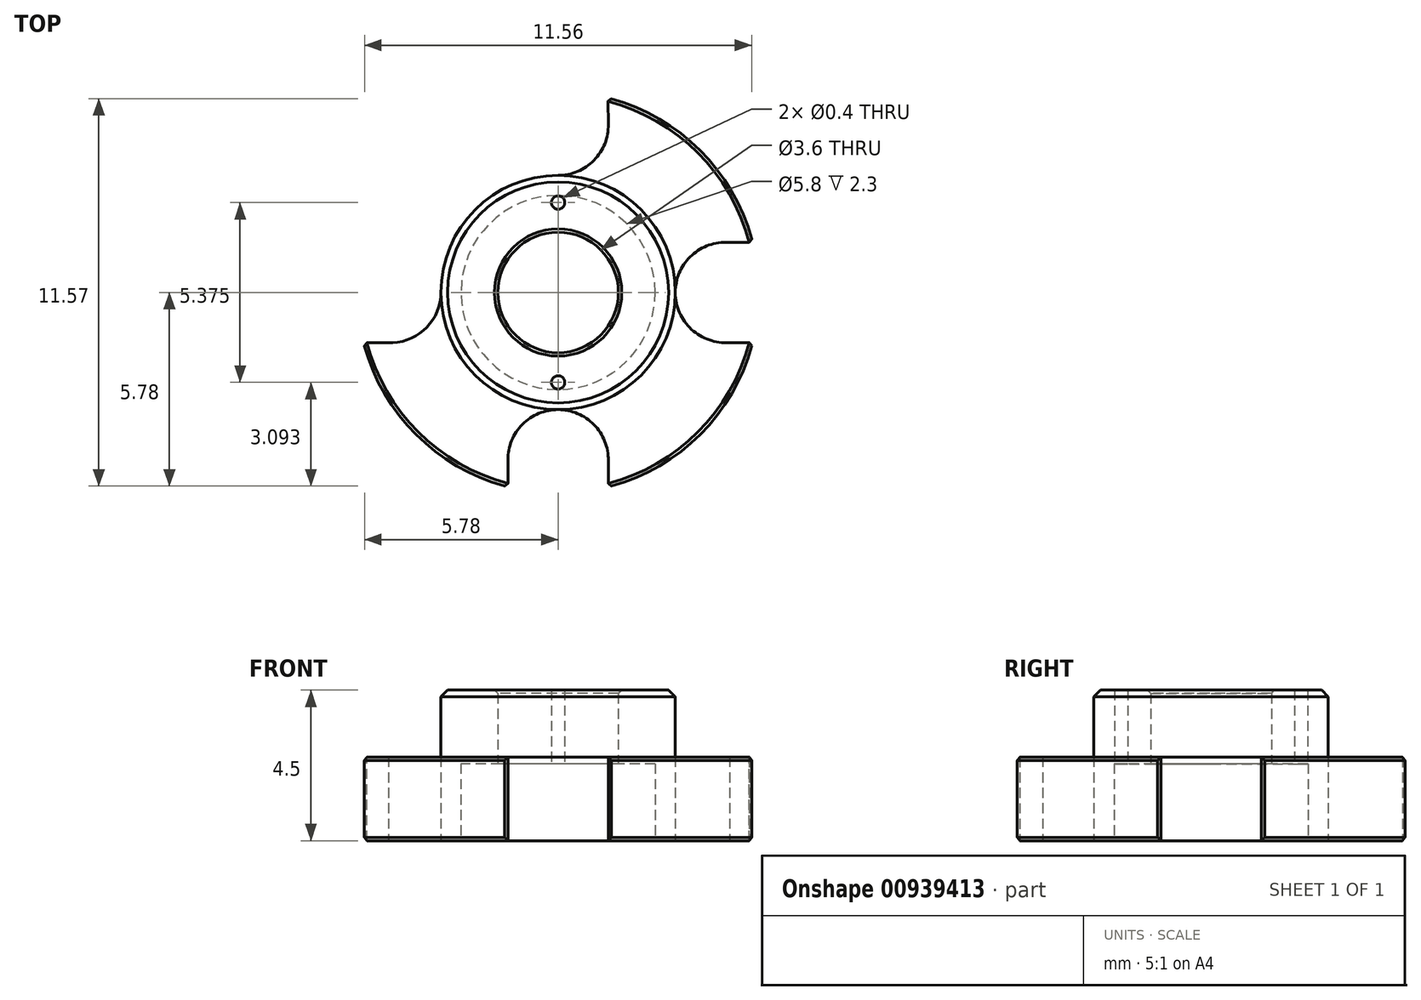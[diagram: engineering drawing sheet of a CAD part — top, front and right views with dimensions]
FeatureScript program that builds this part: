
annotation { "Feature Type Name" : "Feature", "Feature Type Description" : "" }
export const myFeature = defineFeature(function(context is Context, id is Id, definition is map)
    precondition{}
    {
        {
            var Q0;
            Q0=qCreatedBy(makeId("Top.planeOp"),FACE);
            var sketch = newSketch(context, id + "F0", { "sketchPlane" : qUnion([Q0])});
            skCircle(sketch, "E0", {"center": v(0, 0) * mm, "radius": 6 * mm});
            skCircle(sketch, "E1", {"center": v(0, 0) * mm, "radius": 3.5 * mm});
            skCircle(sketch, "E2", {"center": v(0, 0) * mm, "radius": 1.8 * mm});
            skCircle(sketch, "E3", {"center": v(0, 5) * mm, "radius": 1.5 * mm});
            skLineSegment(sketch, "E4", {"start": v(-1.5, 5.01) * mm, "end": v(-1.5, 5.8) * mm});
            skLineSegment(sketch, "E5", {"start": v(1.5, 5.03) * mm, "end": v(1.48, 5.81) * mm});
            skCircle(sketch, "E6", {"center": v(-5, 0) * mm, "radius": 1.5 * mm});
            skLineSegment(sketch, "E7", {"start": v(-4.98, 1.5) * mm, "end": v(-5.8, 1.5) * mm});
            skLineSegment(sketch, "E8", {"start": v(-4.94, -1.5) * mm, "end": v(-5.8, -1.5) * mm});
            skCircle(sketch, "E9", {"center": v(5, 0) * mm, "radius": 1.5 * mm});
            skLineSegment(sketch, "E10", {"start": v(5.01, 1.5) * mm, "end": v(5.8, 1.5) * mm});
            skLineSegment(sketch, "E11", {"start": v(5.12, -1.5) * mm, "end": v(5.81, -1.5) * mm});
            skCircle(sketch, "E12", {"center": v(0, -5) * mm, "radius": 1.5 * mm});
            skLineSegment(sketch, "E13", {"start": v(-1.5, -5) * mm, "end": v(-1.5, -5.8) * mm});
            skLineSegment(sketch, "E14", {"start": v(1.5, -5.02) * mm, "end": v(1.5, -5.8) * mm});
            skCircle(sketch, "E15", {"center": v(0, 0) * mm, "radius": 2.9 * mm});
            skCircle(sketch, "E16", {"center": v(0, 0) * mm, "radius": 2.69 * mm});
            skCircle(sketch, "E17", {"center": v(0, -2.69) * mm, "radius": 0.2 * mm});
            skCircle(sketch, "E18", {"center": v(0, 2.69) * mm, "radius": 0.2 * mm});
            skSolve(sketch);
        }
        {
            var Q0;
            Q0=makeQuery(id+"F0.imprint","IMPRINT",FACE,{"disambiguationData":[TD([[makeQuery(id+"F0.imprint","IMPRINT",EDGE,{"derivedFrom":sQuery(id+"F0.wireOp",EDGE,"E15")}),-1.0]])]});
            var Q1;
            Q1=makeQuery(id+"F0.imprint","IMPRINT",FACE,{"disambiguationData":[TD([[makeQuery(id+"F0.imprint","IMPRINT",EDGE,{"derivedFrom":sQuery(id+"F0.wireOp",EDGE,"E2")}),-1.0]])]});
            var Q2;
            Q2=makeQuery(id+"F0.imprint","IMPRINT",FACE,{"disambiguationData":[TD([[makeQuery(id+"F0.imprint","IMPRINT",EDGE,{"derivedFrom":sQuery(id+"F0.wireOp",EDGE,"E15")}),1.0]])]});
            extrude(context, id + "F1", {"entities" : qUnion([Q0, Q1, Q2]), "depth" : 4.5 * mm, "offsetDistance" : 25 * mm});
        }
        {
            var Q0;
            {var subQ0=sQuery(id+"F0.wireOp",EDGE,"E17");var subQ1=sQuery(id+"F0.wireOp",EDGE,"E15");var subQ2=makeQuery(id+"F0.imprint","INTERSECT",VERTEX,{"derivedFrom":[subQ1,subQ0]});Q0=makeQuery(id+"F0.imprint","IMPRINT",FACE,{"disambiguationData":[TD([[makeQuery(id+"F0.imprint","IMPRINT",EDGE,{"disambiguationData":[TD([[subQ2,-1.0]])],"derivedFrom":subQ1}),1.0]])]});}
            var Q1;
            Q1=makeQuery(id+"F0.imprint","IMPRINT",FACE,{"disambiguationData":[TD([[makeQuery(id+"F0.imprint","IMPRINT",EDGE,{"derivedFrom":sQuery(id+"F0.wireOp",EDGE,"E2")}),-1.0]])]});
            var Q2;
            {var subQ0=sQuery(id+"F0.wireOp",EDGE,"E17");var subQ1=sQuery(id+"F0.wireOp",EDGE,"E15");var subQ2=makeQuery(id+"F0.imprint","INTERSECT",VERTEX,{"derivedFrom":[subQ1,subQ0]});Q2=makeQuery(id+"F0.imprint","IMPRINT",FACE,{"disambiguationData":[TD([[makeQuery(id+"F0.imprint","IMPRINT",EDGE,{"disambiguationData":[TD([[subQ2,1.0]])],"derivedFrom":subQ1}),1.0]])]});}
            extrude(context, id + "F2", {"entities" : qUnion([Q0, Q1, Q2]), "operationType" : NewBodyOperationType.REMOVE, "oppositeDirection" : true, "depth" : -2.3 * mm, "offsetDistance" : 25 * mm});
        }
        {
            var Q0;
            {var subQ0=sQuery(id+"F0.wireOp",EDGE,"E4");Q0=makeQuery(id+"F0.imprint","IMPRINT",FACE,{"disambiguationData":[TD([[makeQuery(id+"F0.imprint","IMPRINT",EDGE,{"derivedFrom":subQ0}),1.0]])]});}
            var Q1;
            {var subQ0=sQuery(id+"F0.wireOp",EDGE,"E5");Q1=makeQuery(id+"F0.imprint","IMPRINT",FACE,{"disambiguationData":[TD([[makeQuery(id+"F0.imprint","IMPRINT",EDGE,{"derivedFrom":subQ0}),-1.0]])]});}
            var Q2;
            {var subQ0=sQuery(id+"F0.wireOp",EDGE,"E11");Q2=makeQuery(id+"F0.imprint","IMPRINT",FACE,{"disambiguationData":[TD([[makeQuery(id+"F0.imprint","IMPRINT",EDGE,{"derivedFrom":subQ0}),-1.0]])]});}
            var Q3;
            {var subQ8=sQuery(id+"F0.wireOp",EDGE,"E13");Q3=makeQuery(id+"F0.imprint","IMPRINT",FACE,{"disambiguationData":[TD([[makeQuery(id+"F0.imprint","IMPRINT",EDGE,{"derivedFrom":subQ8}),-1.0]])]});}
            extrude(context, id + "F3", {"entities" : qUnion([Q0, Q1, Q2, Q3]), "operationType" : NewBodyOperationType.ADD, "depth" : 2.5 * mm, "offsetDistance" : 25 * mm});
        }
        {
            var Q0;
            Q0=makeQuery(id+"F1.opExtrude","CAP_EDGE",EDGE,{"disambiguationData":[OSD([sQuery(id+"F0.wireOp",EDGE,"E1")])],"isStart":false});
            chamfer(context, id + "F4", {"entities" : qUnion([Q0]), "width" : 0.2 * mm, "tangentPropagation" : true});
        }
        {
            var Q0;
            Q0=makeQuery(id+"F3.opExtrude","SWEPT_EDGE",EDGE,{"disambiguationData":[OSD([sQuery(id+"F0.wireOp",EDGE,"E0"),sQuery(id+"F0.wireOp",EDGE,"E4")])]});
            var Q1;
            Q1=makeQuery(id+"F3.opExtrude","SWEPT_EDGE",EDGE,{"disambiguationData":[OSD([sQuery(id+"F0.wireOp",EDGE,"E0"),sQuery(id+"F0.wireOp",EDGE,"E5")])]});
            var Q2;
            Q2=makeQuery(id+"F3.opExtrude","SWEPT_EDGE",EDGE,{"disambiguationData":[OSD([sQuery(id+"F0.wireOp",EDGE,"E0"),sQuery(id+"F0.wireOp",EDGE,"E10")])]});
            var Q3;
            Q3=makeQuery(id+"F3.opExtrude","SWEPT_EDGE",EDGE,{"disambiguationData":[OSD([sQuery(id+"F0.wireOp",EDGE,"E0"),sQuery(id+"F0.wireOp",EDGE,"E11")])]});
            var Q4;
            Q4=makeQuery(id+"F3.opExtrude","SWEPT_EDGE",EDGE,{"disambiguationData":[OSD([sQuery(id+"F0.wireOp",EDGE,"E0"),sQuery(id+"F0.wireOp",EDGE,"E13")])]});
            var Q5;
            Q5=makeQuery(id+"F3.opExtrude","SWEPT_EDGE",EDGE,{"disambiguationData":[OSD([sQuery(id+"F0.wireOp",EDGE,"E0"),sQuery(id+"F0.wireOp",EDGE,"E8")])]});
            var Q6;
            Q6=makeQuery(id+"F3.opExtrude","SWEPT_EDGE",EDGE,{"disambiguationData":[OSD([sQuery(id+"F0.wireOp",EDGE,"E0"),sQuery(id+"F0.wireOp",EDGE,"E14")])]});
            var Q7;
            Q7=makeQuery(id+"F3.opExtrude","SWEPT_EDGE",EDGE,{"disambiguationData":[OSD([sQuery(id+"F0.wireOp",EDGE,"E0"),sQuery(id+"F0.wireOp",EDGE,"E7")])]});
            chamfer(context, id + "F5", {"entities" : qUnion([Q0, Q1, Q2, Q3, Q4, Q5, Q6, Q7]), "width" : 0.1 * mm, "tangentPropagation" : true});
        }
        {
            var Q0;
            Q0=makeQuery(id+"F2.boolean.opBoolean","COPY",EDGE,{"derivedFrom":makeQuery(id+"F2.opExtrude","CAP_EDGE",EDGE,{"disambiguationData":[OSD([sQuery(id+"F0.wireOp",EDGE,"E2")])],"isStart":false})});
            var Q1;
            Q1=makeQuery(id+"F2.boolean.opBoolean","COPY",EDGE,{"derivedFrom":makeQuery(id+"F2.opExtrude","CAP_EDGE",EDGE,{"disambiguationData":[OSD([sQuery(id+"F0.wireOp",EDGE,"E15")])],"isStart":true})});
            var Q2;
            Q2=makeQuery(id+"F1.opExtrude","CAP_EDGE",EDGE,{"disambiguationData":[OSD([sQuery(id+"F0.wireOp",EDGE,"E2")])],"isStart":false});
            var Q3;
            {var subQ0=sQuery(id+"F0.wireOp",EDGE,"E0");Q3=makeQuery(id+"F3.opExtrude","CAP_EDGE",EDGE,{"disambiguationData":[OSD([subQ0]),TDD([makeQuery(id+"F0.imprint","IMPRINT",EDGE,{"disambiguationData":[TD([[makeQuery(id+"F0.imprint","INTERSECT",VERTEX,{"derivedFrom":[subQ0,sQuery(id+"F0.wireOp",EDGE,"E4")]}),-1.0]])],"derivedFrom":subQ0})])],"isStart":false});}
            var Q4;
            {var subQ0=sQuery(id+"F0.wireOp",EDGE,"E0");Q4=makeQuery(id+"F3.opExtrude","CAP_EDGE",EDGE,{"disambiguationData":[OSD([subQ0]),TDD([makeQuery(id+"F0.imprint","IMPRINT",EDGE,{"disambiguationData":[TD([[makeQuery(id+"F0.imprint","INTERSECT",VERTEX,{"derivedFrom":[subQ0,sQuery(id+"F0.wireOp",EDGE,"E5")]}),1.0]])],"derivedFrom":subQ0})])],"isStart":false});}
            var Q5;
            {var subQ0=sQuery(id+"F0.wireOp",EDGE,"E0");Q5=makeQuery(id+"F3.opExtrude","CAP_EDGE",EDGE,{"disambiguationData":[OSD([subQ0]),TDD([makeQuery(id+"F0.imprint","IMPRINT",EDGE,{"disambiguationData":[TD([[makeQuery(id+"F0.imprint","INTERSECT",VERTEX,{"derivedFrom":[subQ0,sQuery(id+"F0.wireOp",EDGE,"E11")]}),1.0]])],"derivedFrom":subQ0})])],"isStart":false});}
            var Q6;
            {var subQ0=sQuery(id+"F0.wireOp",EDGE,"E0");Q6=makeQuery(id+"F3.opExtrude","CAP_EDGE",EDGE,{"disambiguationData":[OSD([subQ0]),TDD([makeQuery(id+"F0.imprint","IMPRINT",EDGE,{"disambiguationData":[TD([[makeQuery(id+"F0.imprint","INTERSECT",VERTEX,{"derivedFrom":[subQ0,sQuery(id+"F0.wireOp",EDGE,"E8")]}),-1.0]])],"derivedFrom":subQ0})])],"isStart":false});}
            var Q7;
            {var subQ0=sQuery(id+"F0.wireOp",EDGE,"E0");Q7=makeQuery(id+"F3.opExtrude","CAP_EDGE",EDGE,{"disambiguationData":[OSD([subQ0]),TDD([makeQuery(id+"F0.imprint","IMPRINT",EDGE,{"disambiguationData":[TD([[makeQuery(id+"F0.imprint","INTERSECT",VERTEX,{"derivedFrom":[subQ0,sQuery(id+"F0.wireOp",EDGE,"E5")]}),1.0]])],"derivedFrom":subQ0})])],"isStart":true});}
            var Q8;
            {var subQ0=sQuery(id+"F0.wireOp",EDGE,"E0");Q8=makeQuery(id+"F3.opExtrude","CAP_EDGE",EDGE,{"disambiguationData":[OSD([subQ0]),TDD([makeQuery(id+"F0.imprint","IMPRINT",EDGE,{"disambiguationData":[TD([[makeQuery(id+"F0.imprint","INTERSECT",VERTEX,{"derivedFrom":[subQ0,sQuery(id+"F0.wireOp",EDGE,"E4")]}),-1.0]])],"derivedFrom":subQ0})])],"isStart":true});}
            var Q9;
            {var subQ0=sQuery(id+"F0.wireOp",EDGE,"E0");Q9=makeQuery(id+"F3.opExtrude","CAP_EDGE",EDGE,{"disambiguationData":[OSD([subQ0]),TDD([makeQuery(id+"F0.imprint","IMPRINT",EDGE,{"disambiguationData":[TD([[makeQuery(id+"F0.imprint","INTERSECT",VERTEX,{"derivedFrom":[subQ0,sQuery(id+"F0.wireOp",EDGE,"E8")]}),-1.0]])],"derivedFrom":subQ0})])],"isStart":true});}
            var Q10;
            {var subQ0=sQuery(id+"F0.wireOp",EDGE,"E0");Q10=makeQuery(id+"F3.opExtrude","CAP_EDGE",EDGE,{"disambiguationData":[OSD([subQ0]),TDD([makeQuery(id+"F0.imprint","IMPRINT",EDGE,{"disambiguationData":[TD([[makeQuery(id+"F0.imprint","INTERSECT",VERTEX,{"derivedFrom":[subQ0,sQuery(id+"F0.wireOp",EDGE,"E11")]}),1.0]])],"derivedFrom":subQ0})])],"isStart":true});}
            chamfer(context, id + "F6", {"entities" : qUnion([Q0, Q1, Q2, Q3, Q4, Q5, Q6, Q7, Q8, Q9, Q10]), "width" : 0.1 * mm, "tangentPropagation" : true});
        }
    });
